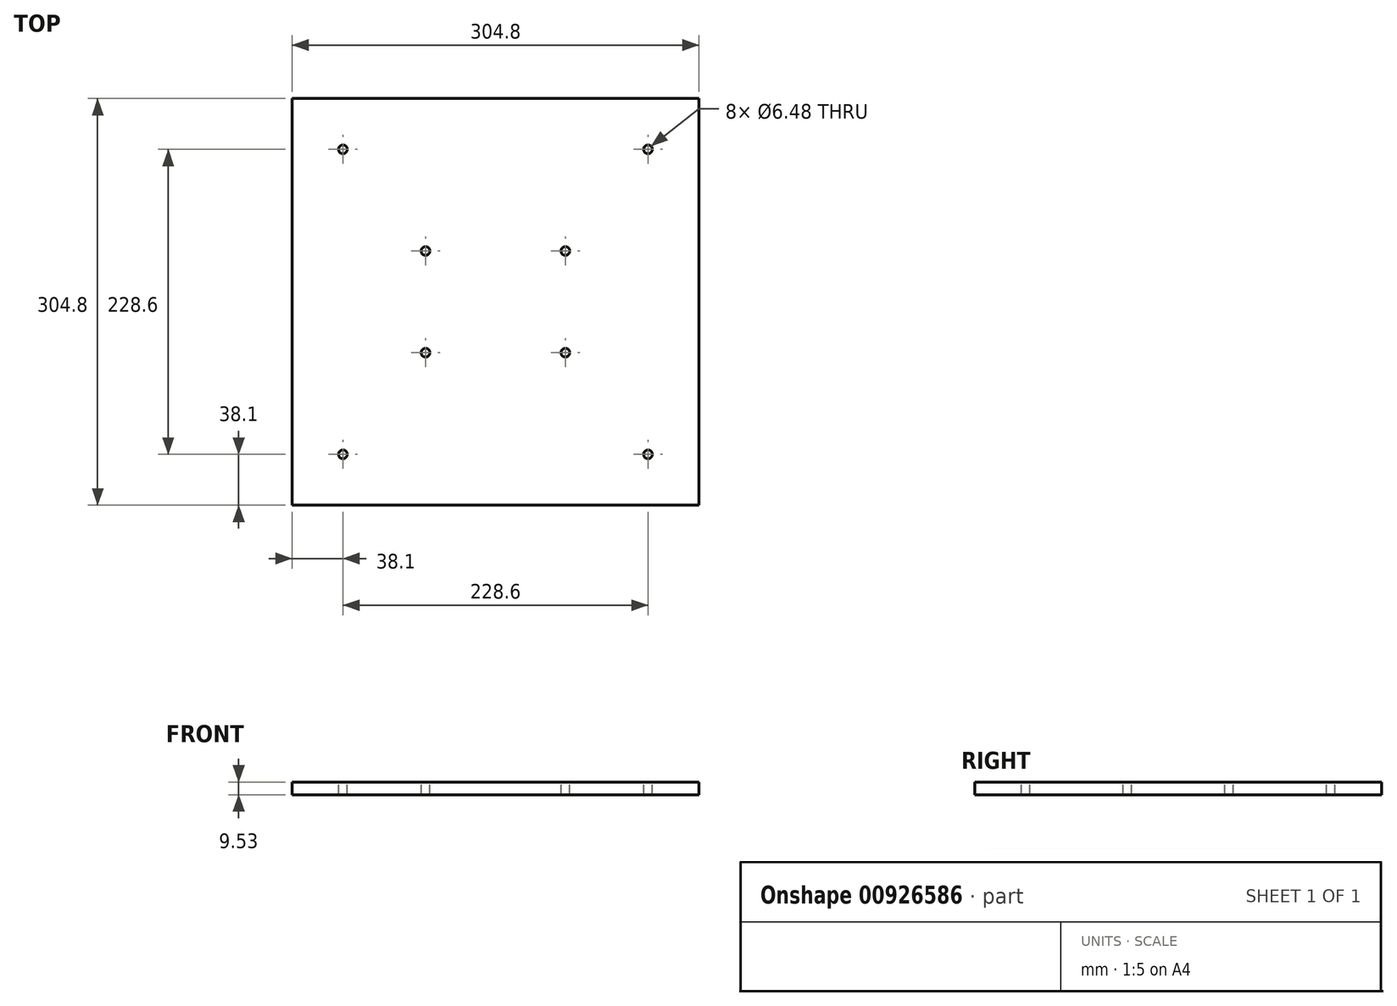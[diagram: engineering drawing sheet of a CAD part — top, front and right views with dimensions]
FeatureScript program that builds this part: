
annotation { "Feature Type Name" : "Feature", "Feature Type Description" : "" }
export const myFeature = defineFeature(function(context is Context, id is Id, definition is map)
    precondition{}
    {
        {
            var Q0;
            Q0=qCreatedBy(makeId("Front.planeOp"),FACE);
            var sketch = newSketch(context, id + "F0", { "sketchPlane" : qUnion([Q0])});
            skLineSegment(sketch, "E0", {"start": v(-142.88, 0) * mm, "end": v(-142.88, 0) * mm});
            skLineSegment(sketch, "E1", {"start": v(-142.88, 0) * mm, "end": v(142.88, 0) * mm});
            skLineSegment(sketch, "E2", {"start": v(142.88, 0) * mm, "end": v(142.88, 0) * mm});
            skLineSegment(sketch, "E3", {"start": v(-142.88, 0) * mm, "end": v(-152.4, 0) * mm});
            skLineSegment(sketch, "E4", {"start": v(-152.4, 0) * mm, "end": v(-152.4, 9.52) * mm});
            skLineSegment(sketch, "E5", {"start": v(-152.4, 9.52) * mm, "end": v(152.4, 9.52) * mm});
            skLineSegment(sketch, "E6", {"start": v(152.4, 9.52) * mm, "end": v(152.4, 0) * mm});
            skLineSegment(sketch, "E7", {"start": v(152.4, 0) * mm, "end": v(142.88, 0) * mm});
            skLineSegment(sketch, "E8", {"start": v(-142.88, 0) * mm, "end": v(0, 0) * mm, "construction": true});
            skLineSegment(sketch, "E9", {"start": v(0, 0) * mm, "end": v(142.88, 0) * mm, "construction": true});
            skSolve(sketch);
        }
        {
            var Q0;
            Q0=makeQuery(id+"F0.imprint","IMPRINT",FACE,{"disambiguationData":[TD([[makeQuery(id+"F0.imprint","IMPRINT",EDGE,{"derivedFrom":sQuery(id+"F0.wireOp",EDGE,"E1")}),1.0]])]});
            extrude(context, id + "F1", {"entities" : qUnion([Q0]), "depth" : 304.8 * mm, "offsetDistance" : 25.4 * mm});
        }
        {
            var Q0;
            Q0=makeQuery(id+"F1.opExtrude","SWEPT_FACE",FACE,{"disambiguationData":[OSD([sQuery(id+"F0.wireOp",EDGE,"E5")])]});
            var sketch = newSketch(context, id + "F2", { "sketchPlane" : qUnion([Q0])});
            skCircle(sketch, "E10", {"center": v(-52.39, -114.3) * mm, "radius": 3.24 * mm});
            skCircle(sketch, "E11.0.1.0", {"center": v(-52.39, -190.5) * mm, "radius": 3.24 * mm});
            skCircle(sketch, "E11.1.0.0", {"center": v(52.39, -114.3) * mm, "radius": 3.24 * mm});
            skCircle(sketch, "E11.1.1.0", {"center": v(52.39, -190.5) * mm, "radius": 3.24 * mm});
            skLineSegment(sketch, "E11.direction1", {"start": v(-52.39, -114.3) * mm, "end": v(52.39, -114.3) * mm, "construction": true});
            skLineSegment(sketch, "E11.direction2", {"start": v(-52.39, -114.3) * mm, "end": v(-52.39, -190.5) * mm, "construction": true});
            skLineSegment(sketch, "E12", {"start": v(-52.39, -114.3) * mm, "end": v(-52.39, 0) * mm, "construction": true});
            skLineSegment(sketch, "E13", {"start": v(-52.39, -190.5) * mm, "end": v(-52.39, -304.8) * mm, "construction": true});
            skLineSegment(sketch, "E14", {"start": v(-52.39, -114.3) * mm, "end": v(-152.4, -114.3) * mm, "construction": true});
            skLineSegment(sketch, "E15", {"start": v(52.39, -114.3) * mm, "end": v(152.4, -114.3) * mm, "construction": true});
            skSolve(sketch);
        }
        {
            var Q0;
            Q0=makeQuery(id+"F2.imprint","IMPRINT",FACE,{"disambiguationData":[TD([[makeQuery(id+"F2.imprint","IMPRINT",EDGE,{"derivedFrom":sQuery(id+"F2.wireOp",EDGE,"E10")}),1.0]])]});
            var Q1;
            Q1=makeQuery(id+"F2.imprint","IMPRINT",FACE,{"disambiguationData":[TD([[makeQuery(id+"F2.imprint","IMPRINT",EDGE,{"derivedFrom":sQuery(id+"F2.wireOp",EDGE,"E11.1.0.0")}),1.0]])]});
            var Q2;
            Q2=makeQuery(id+"F2.imprint","IMPRINT",FACE,{"disambiguationData":[TD([[makeQuery(id+"F2.imprint","IMPRINT",EDGE,{"derivedFrom":sQuery(id+"F2.wireOp",EDGE,"E11.0.1.0")}),1.0]])]});
            var Q3;
            Q3=makeQuery(id+"F2.imprint","IMPRINT",FACE,{"disambiguationData":[TD([[makeQuery(id+"F2.imprint","IMPRINT",EDGE,{"derivedFrom":sQuery(id+"F2.wireOp",EDGE,"E11.1.1.0")}),1.0]])]});
            extrude(context, id + "F3", {"entities" : qUnion([Q0, Q1, Q2, Q3]), "operationType" : NewBodyOperationType.REMOVE, "endBound" : BoundingType.UP_TO_NEXT, "oppositeDirection" : true, "depth" : 25.4 * mm, "offsetDistance" : 25.4 * mm});
        }
        {
            var Q0;
            Q0=makeQuery(id+"F1.opExtrude","SWEPT_FACE",FACE,{"disambiguationData":[OSD([sQuery(id+"F0.wireOp",EDGE,"E5")])]});
            var sketch = newSketch(context, id + "F4", { "sketchPlane" : qUnion([Q0])});
            skCircle(sketch, "E16", {"center": v(-114.3, -38.1) * mm, "radius": 3.24 * mm});
            skCircle(sketch, "E17.0.1.0", {"center": v(-114.3, -266.7) * mm, "radius": 3.24 * mm});
            skCircle(sketch, "E17.1.0.0", {"center": v(114.3, -38.1) * mm, "radius": 3.24 * mm});
            skCircle(sketch, "E17.1.1.0", {"center": v(114.3, -266.7) * mm, "radius": 3.24 * mm});
            skLineSegment(sketch, "E17.direction1", {"start": v(-114.3, -38.1) * mm, "end": v(114.3, -38.1) * mm, "construction": true});
            skLineSegment(sketch, "E17.direction2", {"start": v(-114.3, -38.1) * mm, "end": v(-114.3, -266.7) * mm, "construction": true});
            skLineSegment(sketch, "E18", {"start": v(-114.3, -38.1) * mm, "end": v(-114.3, 0) * mm, "construction": true});
            skLineSegment(sketch, "E19", {"start": v(-114.3, -38.1) * mm, "end": v(-152.4, -38.1) * mm, "construction": true});
            skLineSegment(sketch, "E20", {"start": v(114.3, -38.1) * mm, "end": v(152.4, -38.1) * mm, "construction": true});
            skLineSegment(sketch, "E21", {"start": v(-114.3, -266.7) * mm, "end": v(-114.3, -304.8) * mm, "construction": true});
            skSolve(sketch);
        }
        {
            var Q0;
            Q0=makeQuery(id+"F4.imprint","IMPRINT",FACE,{"disambiguationData":[TD([[makeQuery(id+"F4.imprint","IMPRINT",EDGE,{"derivedFrom":sQuery(id+"F4.wireOp",EDGE,"E16")}),1.0]])]});
            var Q1;
            Q1=makeQuery(id+"F4.imprint","IMPRINT",FACE,{"disambiguationData":[TD([[makeQuery(id+"F4.imprint","IMPRINT",EDGE,{"derivedFrom":sQuery(id+"F4.wireOp",EDGE,"E17.1.0.0")}),1.0]])]});
            var Q2;
            Q2=makeQuery(id+"F4.imprint","IMPRINT",FACE,{"disambiguationData":[TD([[makeQuery(id+"F4.imprint","IMPRINT",EDGE,{"derivedFrom":sQuery(id+"F4.wireOp",EDGE,"E17.0.1.0")}),1.0]])]});
            var Q3;
            Q3=makeQuery(id+"F4.imprint","IMPRINT",FACE,{"disambiguationData":[TD([[makeQuery(id+"F4.imprint","IMPRINT",EDGE,{"derivedFrom":sQuery(id+"F4.wireOp",EDGE,"E17.1.1.0")}),1.0]])]});
            extrude(context, id + "F5", {"entities" : qUnion([Q0, Q1, Q2, Q3]), "operationType" : NewBodyOperationType.REMOVE, "endBound" : BoundingType.UP_TO_NEXT, "oppositeDirection" : true, "depth" : 25.4 * mm, "offsetDistance" : 25.4 * mm});
        }
        {
            var Q0;
            Q0=qCreatedBy(makeId("Front.planeOp"),FACE);
            var sketch = newSketch(context, id + "F6", { "sketchPlane" : qUnion([Q0])});
            skLineSegment(sketch, "E22.bottom", {"start": v(241.52, 240.9) * mm, "end": v(-63.28, 240.9) * mm});
            skLineSegment(sketch, "E22.top", {"start": v(241.52, -63.9) * mm, "end": v(-63.28, -63.9) * mm});
            skLineSegment(sketch, "E22.left", {"start": v(241.52, 240.9) * mm, "end": v(241.52, -63.9) * mm});
            skLineSegment(sketch, "E22.right", {"start": v(-63.28, 240.9) * mm, "end": v(-63.28, -63.9) * mm});
            skSolve(sketch);
        }
        {
            var Q0;
            Q0=makeQuery(id+"F1.opExtrude","SWEPT_FACE",FACE,{"disambiguationData":[OSD([sQuery(id+"F0.wireOp",EDGE,"E4")])]});
            var sketch = newSketch(context, id + "F7", { "sketchPlane" : qUnion([Q0])});
            skCircle(sketch, "E23", {"center": v(38.1, 37.7) * mm, "radius": 6.35 * mm});
            skCircle(sketch, "E24", {"center": v(266.71, 37.7) * mm, "radius": 6.35 * mm});
            skLineSegment(sketch, "E25", {"start": v(0, 37.7) * mm, "end": v(38.1, 37.7) * mm, "construction": true});
            skLineSegment(sketch, "E26", {"start": v(266.71, 37.7) * mm, "end": v(304.8, 38.76) * mm, "construction": true});
            skLineSegment(sketch, "E27", {"start": v(266.71, 37.7) * mm, "end": v(266.71, 0) * mm, "construction": true});
            skLineSegment(sketch, "E28", {"start": v(38.1, 37.7) * mm, "end": v(38.1, 0) * mm, "construction": true});
            skSolve(sketch);
        }
        {
            var Q0;
            Q0=makeQuery(id+"F7.imprint","IMPRINT",FACE,{"disambiguationData":[TD([[makeQuery(id+"F7.imprint","IMPRINT",EDGE,{"derivedFrom":sQuery(id+"F7.wireOp",EDGE,"E23")}),-1.0]])]});
            var Q1;
            Q1=makeQuery(id+"F7.imprint","IMPRINT",FACE,{"disambiguationData":[TD([[makeQuery(id+"F7.imprint","IMPRINT",EDGE,{"derivedFrom":sQuery(id+"F7.wireOp",EDGE,"E24")}),1.0]])]});
            extrude(context, id + "F8", {"entities" : qUnion([Q0, Q1]), "operationType" : NewBodyOperationType.REMOVE, "endBound" : BoundingType.THROUGH_ALL, "oppositeDirection" : true, "depth" : 25.4 * mm, "offsetDistance" : 25.4 * mm});
        }
        {
            var Q0;
            Q0=makeQuery(id+"F1.opExtrude","SWEPT_FACE",FACE,{"disambiguationData":[OSD([sQuery(id+"F0.wireOp",EDGE,"E4")])]});
            var sketch = newSketch(context, id + "F9", { "sketchPlane" : qUnion([Q0])});
            skCircle(sketch, "E29", {"center": v(100.01, 247.65) * mm, "radius": 4.78 * mm});
            skCircle(sketch, "E30", {"center": v(204.79, 247.65) * mm, "radius": 4.78 * mm});
            skCircle(sketch, "E31", {"center": v(100.01, 228.6) * mm, "radius": 4.78 * mm});
            skCircle(sketch, "E32", {"center": v(204.79, 228.6) * mm, "radius": 4.78 * mm});
            skLineSegment(sketch, "E33", {"start": v(0, 247.65) * mm, "end": v(100.01, 247.65) * mm, "construction": true});
            skLineSegment(sketch, "E34", {"start": v(0, 228.6) * mm, "end": v(100.01, 228.6) * mm, "construction": true});
            skLineSegment(sketch, "E35", {"start": v(204.79, 247.65) * mm, "end": v(304.8, 247.65) * mm, "construction": true});
            skLineSegment(sketch, "E36", {"start": v(204.79, 228.6) * mm, "end": v(304.8, 228.6) * mm, "construction": true});
            skLineSegment(sketch, "E37", {"start": v(100.01, 247.65) * mm, "end": v(204.79, 247.65) * mm, "construction": true});
            skLineSegment(sketch, "E38", {"start": v(100.01, 228.6) * mm, "end": v(204.79, 228.6) * mm, "construction": true});
            skLineSegment(sketch, "E39", {"start": v(100.01, 247.65) * mm, "end": v(100.01, 228.6) * mm, "construction": true});
            skCircle(sketch, "E40", {"center": v(100.01, 209.55) * mm, "radius": 4.78 * mm});
            skCircle(sketch, "E41", {"center": v(204.79, 209.55) * mm, "radius": 4.78 * mm});
            skLineSegment(sketch, "E42", {"start": v(100.01, 228.6) * mm, "end": v(100.01, 209.55) * mm, "construction": true});
            skLineSegment(sketch, "E43", {"start": v(100.01, 209.55) * mm, "end": v(204.79, 209.55) * mm, "construction": true});
            skSolve(sketch);
        }
        {
            var Q0;
            Q0=makeQuery(id+"F9.imprint","IMPRINT",FACE,{"disambiguationData":[TD([[makeQuery(id+"F9.imprint","IMPRINT",EDGE,{"derivedFrom":sQuery(id+"F9.wireOp",EDGE,"E29")}),1.0]])]});
            var Q1;
            Q1=makeQuery(id+"F9.imprint","IMPRINT",FACE,{"disambiguationData":[TD([[makeQuery(id+"F9.imprint","IMPRINT",EDGE,{"derivedFrom":sQuery(id+"F9.wireOp",EDGE,"E30")}),1.0]])]});
            var Q2;
            Q2=makeQuery(id+"F9.imprint","IMPRINT",FACE,{"disambiguationData":[TD([[makeQuery(id+"F9.imprint","IMPRINT",EDGE,{"derivedFrom":sQuery(id+"F9.wireOp",EDGE,"E31")}),1.0]])]});
            var Q3;
            Q3=makeQuery(id+"F9.imprint","IMPRINT",FACE,{"disambiguationData":[TD([[makeQuery(id+"F9.imprint","IMPRINT",EDGE,{"derivedFrom":sQuery(id+"F9.wireOp",EDGE,"E32")}),1.0]])]});
            var Q4;
            Q4=makeQuery(id+"F9.imprint","IMPRINT",FACE,{"disambiguationData":[TD([[makeQuery(id+"F9.imprint","IMPRINT",EDGE,{"derivedFrom":sQuery(id+"F9.wireOp",EDGE,"E40")}),1.0]])]});
            var Q5;
            Q5=makeQuery(id+"F9.imprint","IMPRINT",FACE,{"disambiguationData":[TD([[makeQuery(id+"F9.imprint","IMPRINT",EDGE,{"derivedFrom":sQuery(id+"F9.wireOp",EDGE,"E41")}),1.0]])]});
            extrude(context, id + "F10", {"entities" : qUnion([Q0, Q1, Q2, Q3, Q4, Q5]), "operationType" : NewBodyOperationType.REMOVE, "endBound" : BoundingType.THROUGH_ALL, "oppositeDirection" : true, "depth" : 25.4 * mm, "offsetDistance" : 25.4 * mm});
        }
    });
